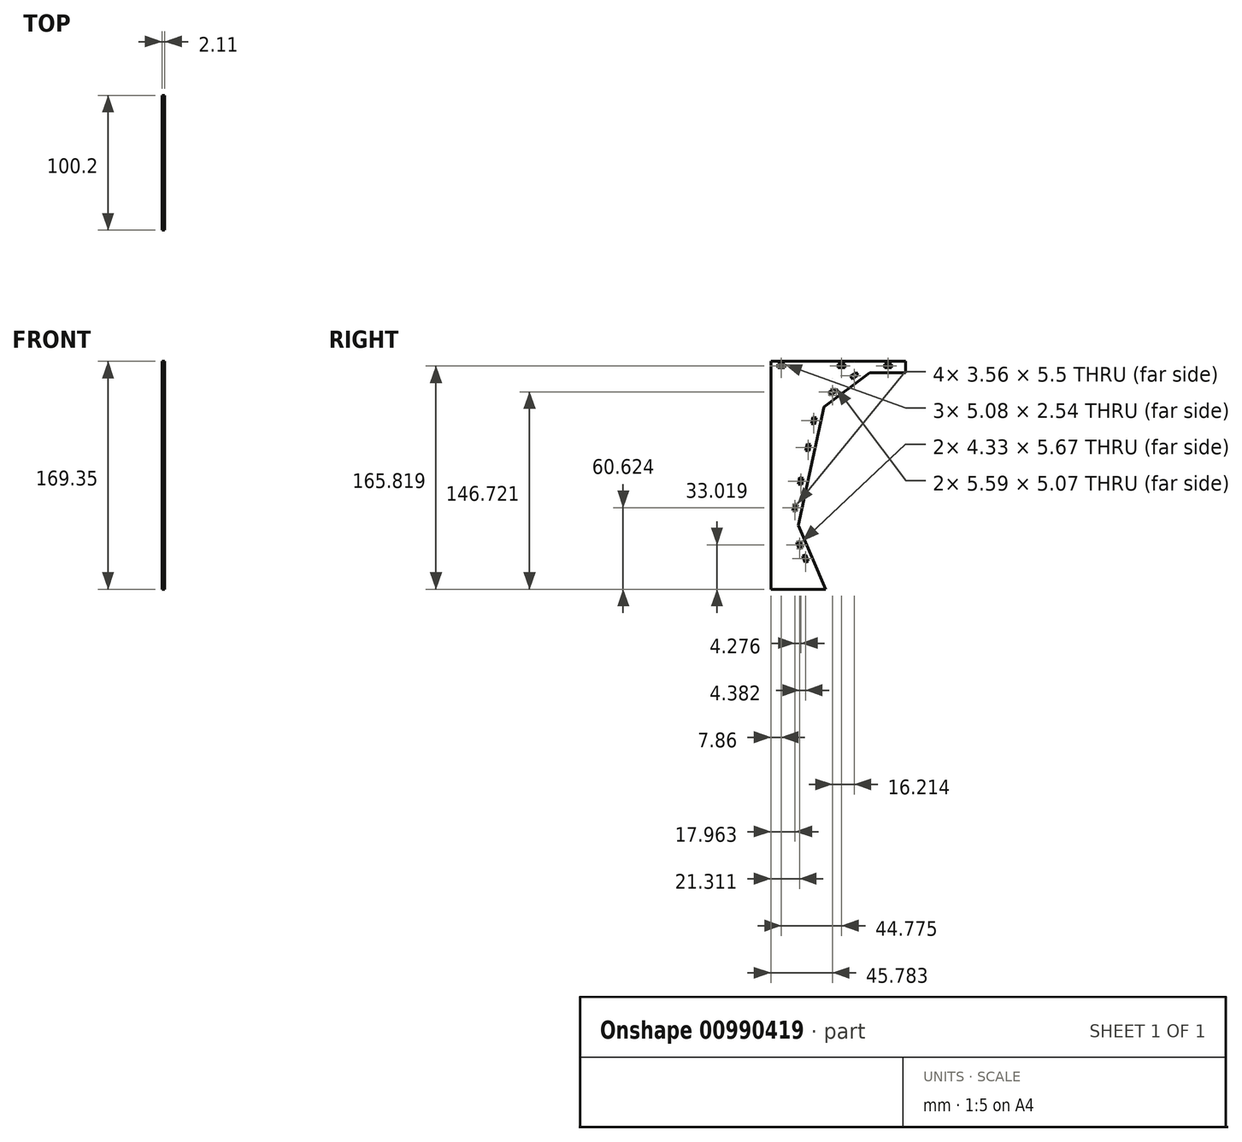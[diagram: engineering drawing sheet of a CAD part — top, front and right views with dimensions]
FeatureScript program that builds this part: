
annotation { "Feature Type Name" : "Feature", "Feature Type Description" : "" }
export const myFeature = defineFeature(function(context is Context, id is Id, definition is map)
    precondition{}
    {
        {
            var Q0;
            Q0=qCreatedBy(makeId("Right.planeOp"),FACE);
            var sketch = newSketch(context, id + "F0", { "sketchPlane" : qUnion([Q0])});
            skLineSegment(sketch, "E0", {"start": v(0, 0) * mm, "end": v(0, 169.34) * mm});
            skLineSegment(sketch, "E1", {"start": v(0, 169.34) * mm, "end": v(200.4, 169.34) * mm});
            skLineSegment(sketch, "E2", {"start": v(0, 0) * mm, "end": v(43.05, 0) * mm, "construction": true});
            skLineSegment(sketch, "E3", {"start": v(43.05, 0) * mm, "end": v(23.47, 45.96) * mm});
            skLineSegment(sketch, "E4", {"start": v(0, 47.82) * mm, "end": v(22.68, 47.82) * mm, "construction": true});
            skLineSegment(sketch, "E5", {"start": v(22.68, 47.82) * mm, "end": v(22.68, 0) * mm, "construction": true});
            skLineSegment(sketch, "E6", {"start": v(23.1, 49.8) * mm, "end": v(40.9, 132) * mm});
            skLineSegment(sketch, "E7", {"start": v(41.4, 134.33) * mm, "end": v(0, 134.33) * mm, "construction": true});
            skLineSegment(sketch, "E8", {"start": v(41.4, 134.33) * mm, "end": v(43.05, 0) * mm, "construction": true});
            skLineSegment(sketch, "E9", {"start": v(43.31, 135.75) * mm, "end": v(72.51, 157.5) * mm});
            skLineSegment(sketch, "E10", {"start": v(74.2, 158.76) * mm, "end": v(74.2, 169.34) * mm, "construction": true});
            skLineSegment(sketch, "E11", {"start": v(74.2, 158.76) * mm, "end": v(0, 158.76) * mm, "construction": true});
            skPoint(sketch, "E12", {"position": v(100.2, 169.34) * mm});
            skLineSegment(sketch, "E13", {"start": v(100.2, 169.34) * mm, "end": v(100.2, 154.3) * mm, "construction": true});
            skLineSegment(sketch, "E14", {"start": v(76.3, 158.76) * mm, "end": v(100.2, 158.76) * mm});
            skLineSegment(sketch, "E15.4", {"start": v(41.18, -0.8) * mm, "end": v(20.56, 47.62) * mm, "construction": true});
            skLineSegment(sketch, "E15.5", {"start": v(20.56, 47.62) * mm, "end": v(39.58, 135.5) * mm});
            skLineSegment(sketch, "E15.6", {"start": v(39.58, 135.5) * mm, "end": v(73.52, 160.79) * mm});
            skLineSegment(sketch, "E15.7", {"start": v(73.52, 160.79) * mm, "end": v(100.2, 160.79) * mm});
            skLineSegment(sketch, "E16.5", {"start": v(11.62, 46.77) * mm, "end": v(31.89, 140.45) * mm});
            skLineSegment(sketch, "E16.6", {"start": v(31.89, 140.45) * mm, "end": v(70.69, 169.35) * mm, "construction": true});
            skLineSegment(sketch, "E16.7", {"start": v(70.69, 169.35) * mm, "end": v(100.2, 169.35) * mm});
            skLineSegment(sketch, "E17", {"start": v(31.89, 140.45) * mm, "end": v(38.14, 169.34) * mm, "construction": true});
            skLineSegment(sketch, "E18", {"start": v(10.6, 158.76) * mm, "end": v(0, 158.76) * mm, "construction": true});
            skLineSegment(sketch, "E19", {"start": v(10.6, 158.76) * mm, "end": v(10.6, 46.77) * mm});
            skLineSegment(sketch, "E20", {"start": v(10.6, 46.77) * mm, "end": v(11.62, 46.77) * mm});
            skLineSegment(sketch, "E21", {"start": v(36.3, 160.79) * mm, "end": v(31.89, 140.45) * mm, "construction": true});
            skLineSegment(sketch, "E22", {"start": v(41.4, 134.33) * mm, "end": v(48.98, 169.34) * mm, "construction": true});
            skLineSegment(sketch, "E23", {"start": v(47.13, 160.79) * mm, "end": v(44.8, 150.07) * mm});
            skLineSegment(sketch, "E24", {"start": v(13.2, 0) * mm, "end": v(0, 0) * mm});
            skLineSegment(sketch, "E25", {"start": v(31.54, 0) * mm, "end": v(43.05, 0) * mm});
            skLineSegment(sketch, "E26", {"start": v(100.2, 158.76) * mm, "end": v(100.2, 169.35) * mm});
            skPoint(sketch, "E27", {"position": v(46.69, 158.76) * mm});
            skPoint(sketch, "E28", {"position": v(56.47, 158.76) * mm});
            skLineSegment(sketch, "E29", {"start": v(46.69, 158.76) * mm, "end": v(56.47, 158.76) * mm});
            skLineSegment(sketch, "E30", {"start": v(44.8, 150.07) * mm, "end": v(46.69, 158.76) * mm});
            skLineSegment(sketch, "E31", {"start": v(10.6, 158.76) * mm, "end": v(35.85, 158.76) * mm});
            skLineSegment(sketch, "E32", {"start": v(35.85, 158.76) * mm, "end": v(31.89, 140.45) * mm});
            skLineSegment(sketch, "E33", {"start": v(44.8, 150.07) * mm, "end": v(56.47, 158.76) * mm});
            skLineSegment(sketch, "E34", {"start": v(30.88, 85.7) * mm, "end": v(20.53, 87.94) * mm, "construction": true});
            skLineSegment(sketch, "E35.0", {"start": v(33.3, -4.15) * mm, "end": v(12.94, 43.67) * mm, "construction": true});
            skLineSegment(sketch, "E36", {"start": v(22.68, 47.82) * mm, "end": v(18.8, 29.9) * mm, "construction": true});
            skLineSegment(sketch, "E37", {"start": v(18.8, 29.9) * mm, "end": v(12.34, 0) * mm});
            skLineSegment(sketch, "E38", {"start": v(18.8, 29.9) * mm, "end": v(31.54, 0) * mm});
            skLineSegment(sketch, "E39", {"start": v(12.34, 0) * mm, "end": v(31.54, 0) * mm});
            skLineSegment(sketch, "E40", {"start": v(20.56, 47.62) * mm, "end": v(40.84, 0) * mm});
            skPoint(sketch, "E41.visualSharp", {"position": v(41.4, 134.33) * mm});
            skArc(sketch, "E41.filletArc", {"start": v(43.31, 135.75) * mm, "mid": v(41.77, 134.1) * mm, "end": v(40.9, 132) * mm});
            skPoint(sketch, "E42.visualSharp", {"position": v(22.68, 47.82) * mm});
            skArc(sketch, "E42.filletArc", {"start": v(23.1, 49.8) * mm, "mid": v(23, 47.85) * mm, "end": v(23.47, 45.96) * mm});
            skPoint(sketch, "E43.visualSharp", {"position": v(74.2, 158.76) * mm});
            skArc(sketch, "E43.filletArc", {"start": v(76.3, 158.76) * mm, "mid": v(74.3, 158.44) * mm, "end": v(72.51, 157.5) * mm});
            skPoint(sketch, "E44", {"position": v(21.75, 93.6) * mm});
            skLineSegment(sketch, "E45", {"start": v(21.75, 93.6) * mm, "end": v(22.1, 95.21) * mm});
            skLineSegment(sketch, "E46", {"start": v(22.1, 95.21) * mm, "end": v(26.54, 94.25) * mm});
            skLineSegment(sketch, "E47", {"start": v(29.56, 96.2) * mm, "end": v(37.5, 132.86) * mm});
            skLineSegment(sketch, "E48", {"start": v(35.55, 135.88) * mm, "end": v(31.1, 136.84) * mm});
            skPoint(sketch, "E49.visualSharp", {"position": v(38.03, 135.35) * mm});
            skArc(sketch, "E49.filletArc", {"start": v(37.5, 132.86) * mm, "mid": v(37.15, 134.78) * mm, "end": v(35.55, 135.88) * mm});
            skPoint(sketch, "E50.visualSharp", {"position": v(29.02, 93.72) * mm});
            skArc(sketch, "E50.filletArc", {"start": v(26.54, 94.25) * mm, "mid": v(28.45, 94.6) * mm, "end": v(29.56, 96.2) * mm});
            skLineSegment(sketch, "E51", {"start": v(21.75, 93.6) * mm, "end": v(32.1, 91.37) * mm, "construction": true});
            skLineSegment(sketch, "E52.0", {"start": v(35.01, 133.4) * mm, "end": v(30.57, 134.36) * mm});
            skLineSegment(sketch, "E52.1", {"start": v(22.64, 97.7) * mm, "end": v(27.08, 96.74) * mm});
            skLineSegment(sketch, "E52.2", {"start": v(27.08, 96.74) * mm, "end": v(27.08, 96.74) * mm});
            skLineSegment(sketch, "E52.3", {"start": v(27.08, 96.74) * mm, "end": v(35.01, 133.4) * mm});
            skLineSegment(sketch, "E52.4", {"start": v(35.01, 133.4) * mm, "end": v(35.01, 133.4) * mm});
            skLineSegment(sketch, "E53.MirrorCS", {"start": v(21.4, 92) * mm, "end": v(25.85, 91.04) * mm});
            skArc(sketch, "E54.MirrorCS", {"start": v(25.85, 91.04) * mm, "mid": v(27.44, 89.94) * mm, "end": v(27.8, 88.02) * mm});
            skLineSegment(sketch, "E55.MirrorCS", {"start": v(27.8, 88.02) * mm, "end": v(19.86, 51.36) * mm});
            skArc(sketch, "E56.MirrorCS", {"start": v(19.86, 51.36) * mm, "mid": v(18.75, 49.76) * mm, "end": v(16.84, 49.41) * mm});
            skLineSegment(sketch, "E57.MirrorCS", {"start": v(16.84, 49.41) * mm, "end": v(12.4, 50.38) * mm});
            skLineSegment(sketch, "E58.MirrorCS", {"start": v(17.37, 51.9) * mm, "end": v(12.94, 52.86) * mm});
            skLineSegment(sketch, "E59.MirrorCS", {"start": v(25.3, 88.56) * mm, "end": v(17.37, 51.9) * mm});
            skLineSegment(sketch, "E60.MirrorCS", {"start": v(20.87, 89.52) * mm, "end": v(25.3, 88.56) * mm});
            skLineSegment(sketch, "E61", {"start": v(33.72, 127.42) * mm, "end": v(31.23, 127.96) * mm});
            skLineSegment(sketch, "E62", {"start": v(31.23, 127.96) * mm, "end": v(30.16, 123) * mm});
            skLineSegment(sketch, "E63", {"start": v(30.16, 123) * mm, "end": v(32.64, 122.46) * mm});
            skLineSegment(sketch, "E64", {"start": v(28.37, 102.7) * mm, "end": v(25.88, 103.24) * mm});
            skLineSegment(sketch, "E65", {"start": v(25.88, 103.24) * mm, "end": v(26.96, 108.2) * mm});
            skLineSegment(sketch, "E66", {"start": v(26.96, 108.2) * mm, "end": v(29.44, 107.66) * mm});
            skLineSegment(sketch, "E67.MirrorCS", {"start": v(24.02, 82.6) * mm, "end": v(21.54, 83.13) * mm});
            skLineSegment(sketch, "E68.MirrorCS", {"start": v(21.54, 83.13) * mm, "end": v(20.46, 78.17) * mm});
            skLineSegment(sketch, "E69.MirrorCS", {"start": v(20.46, 78.17) * mm, "end": v(22.94, 77.63) * mm});
            skLineSegment(sketch, "E70.MirrorCS", {"start": v(17.26, 63.37) * mm, "end": v(19.74, 62.84) * mm});
            skLineSegment(sketch, "E71.MirrorCS", {"start": v(16.19, 58.4) * mm, "end": v(17.26, 63.37) * mm});
            skLineSegment(sketch, "E72.MirrorCS", {"start": v(18.67, 57.87) * mm, "end": v(16.19, 58.4) * mm});
            skLineSegment(sketch, "E73", {"start": v(31.89, 140.45) * mm, "end": v(41.4, 134.33) * mm, "construction": true});
            skLineSegment(sketch, "E74.MirrorCS", {"start": v(37.56, 139.02) * mm, "end": v(34.85, 142.66) * mm});
            skArc(sketch, "E75.MirrorCS", {"start": v(41.12, 138.5) * mm, "mid": v(39.23, 138.02) * mm, "end": v(37.56, 139.02) * mm});
            skLineSegment(sketch, "E76.MirrorCS", {"start": v(71.2, 160.9) * mm, "end": v(41.12, 138.5) * mm});
            skArc(sketch, "E77.MirrorCS", {"start": v(71.72, 164.46) * mm, "mid": v(72.2, 162.57) * mm, "end": v(71.2, 160.9) * mm});
            skLineSegment(sketch, "E78.MirrorCS", {"start": v(69, 168.1) * mm, "end": v(71.72, 164.46) * mm});
            skLineSegment(sketch, "E79.MirrorCS", {"start": v(66.97, 166.58) * mm, "end": v(69.69, 162.94) * mm});
            skLineSegment(sketch, "E80.MirrorCS", {"start": v(69.69, 162.94) * mm, "end": v(39.6, 140.53) * mm});
            skLineSegment(sketch, "E81.MirrorCS", {"start": v(64.8, 159.3) * mm, "end": v(63.28, 161.33) * mm});
            skLineSegment(sketch, "E82.MirrorCS", {"start": v(63.28, 161.33) * mm, "end": v(59.2, 158.3) * mm});
            skLineSegment(sketch, "E83.MirrorCS", {"start": v(59.2, 158.3) * mm, "end": v(60.72, 156.26) * mm});
            skLineSegment(sketch, "E84.MirrorCS", {"start": v(47.06, 149.26) * mm, "end": v(48.58, 147.22) * mm});
            skLineSegment(sketch, "E85.MirrorCS", {"start": v(42.99, 146.22) * mm, "end": v(47.06, 149.26) * mm});
            skLineSegment(sketch, "E86.MirrorCS", {"start": v(44.5, 144.19) * mm, "end": v(42.99, 146.22) * mm});
            skLineSegment(sketch, "E87.MirrorCS", {"start": v(39.6, 140.53) * mm, "end": v(36.89, 144.18) * mm});
            skLineSegment(sketch, "E88", {"start": v(70.69, 169.35) * mm, "end": v(70.69, 164.55) * mm});
            skLineSegment(sketch, "E89", {"start": v(68.15, 162) * mm, "end": v(0, 162) * mm});
            skPoint(sketch, "E90.visualSharp", {"position": v(70.69, 162) * mm});
            skArc(sketch, "E90.filletArc", {"start": v(68.15, 162) * mm, "mid": v(69.94, 162.75) * mm, "end": v(70.69, 164.55) * mm});
            skLineSegment(sketch, "E91.0", {"start": v(68.15, 164.55) * mm, "end": v(0, 164.55) * mm});
            skLineSegment(sketch, "E91.1", {"start": v(68.15, 169.63) * mm, "end": v(68.15, 164.55) * mm});
            skLineSegment(sketch, "E92", {"start": v(55.17, 164.55) * mm, "end": v(55.17, 167.09) * mm});
            skLineSegment(sketch, "E93", {"start": v(55.17, 167.09) * mm, "end": v(50.1, 167.09) * mm});
            skLineSegment(sketch, "E94", {"start": v(50.1, 167.09) * mm, "end": v(50.1, 164.55) * mm});
            skLineSegment(sketch, "E95", {"start": v(10.4, 164.55) * mm, "end": v(10.4, 167.09) * mm});
            skLineSegment(sketch, "E96", {"start": v(10.4, 167.09) * mm, "end": v(5.32, 167.09) * mm});
            skLineSegment(sketch, "E97", {"start": v(5.32, 167.09) * mm, "end": v(5.32, 164.55) * mm});
            skLineSegment(sketch, "E98", {"start": v(22.68, 47.82) * mm, "end": v(11.62, 46.77) * mm, "construction": true});
            skLineSegment(sketch, "E99", {"start": v(15.36, 37.97) * mm, "end": v(19.78, 39.85) * mm});
            skLineSegment(sketch, "E100", {"start": v(23.11, 38.51) * mm, "end": v(37.3, 5.2) * mm});
            skLineSegment(sketch, "E101", {"start": v(35.96, 1.87) * mm, "end": v(31.54, -0.01) * mm});
            skPoint(sketch, "E102.visualSharp", {"position": v(38.3, 2.87) * mm});
            skArc(sketch, "E102.filletArc", {"start": v(35.96, 1.87) * mm, "mid": v(37.32, 3.26) * mm, "end": v(37.3, 5.2) * mm});
            skPoint(sketch, "E103.visualSharp", {"position": v(22.12, 40.85) * mm});
            skArc(sketch, "E103.filletArc", {"start": v(23.11, 38.51) * mm, "mid": v(21.72, 39.87) * mm, "end": v(19.78, 39.85) * mm});
            skLineSegment(sketch, "E104.0", {"start": v(34.97, 4.2) * mm, "end": v(25.52, 0.18) * mm});
            skLineSegment(sketch, "E104.1", {"start": v(20.78, 37.52) * mm, "end": v(34.97, 4.2) * mm});
            skLineSegment(sketch, "E104.2", {"start": v(16.36, 35.63) * mm, "end": v(20.78, 37.52) * mm});
            skLineSegment(sketch, "E105", {"start": v(27.86, 20.9) * mm, "end": v(25.52, 19.9) * mm});
            skLineSegment(sketch, "E106", {"start": v(25.52, 19.9) * mm, "end": v(23.53, 24.57) * mm});
            skLineSegment(sketch, "E107", {"start": v(23.53, 24.57) * mm, "end": v(25.87, 25.57) * mm});
            skLineSegment(sketch, "E108", {"start": v(21.48, 35.85) * mm, "end": v(19.15, 34.86) * mm});
            skLineSegment(sketch, "E109", {"start": v(19.15, 34.86) * mm, "end": v(21.14, 30.18) * mm});
            skLineSegment(sketch, "E110", {"start": v(21.14, 30.18) * mm, "end": v(23.48, 31.18) * mm});
            skLineSegment(sketch, "E111", {"start": v(79.6, 169.35) * mm, "end": v(79.6, 164.55) * mm});
            skLineSegment(sketch, "E112", {"start": v(82.14, 162) * mm, "end": v(100.2, 162) * mm});
            skPoint(sketch, "E113.visualSharp", {"position": v(79.6, 162) * mm});
            skArc(sketch, "E113.filletArc", {"start": v(79.6, 164.55) * mm, "mid": v(80.34, 162.75) * mm, "end": v(82.14, 162) * mm});
            skLineSegment(sketch, "E114.0", {"start": v(82.14, 164.55) * mm, "end": v(100.2, 164.55) * mm});
            skLineSegment(sketch, "E114.1", {"start": v(82.14, 169.35) * mm, "end": v(82.14, 164.55) * mm});
            skLineSegment(sketch, "E115", {"start": v(84.57, 164.55) * mm, "end": v(84.57, 167.09) * mm});
            skPoint(sketch, "E115.endSnap0", {"position": v(68.15, 167.09) * mm});
            skLineSegment(sketch, "E116", {"start": v(84.57, 167.09) * mm, "end": v(89.65, 167.09) * mm});
            skLineSegment(sketch, "E117", {"start": v(89.65, 167.09) * mm, "end": v(89.65, 164.55) * mm});
            skSolve(sketch);
        }
        {
            var Q0;
            Q0=makeQuery(id+"F0.imprint","IMPRINT",FACE,{"disambiguationData":[TD([[makeQuery(id+"F0.imprint","IMPRINT",EDGE,{"derivedFrom":sQuery(id+"F0.wireOp",EDGE,"E19")}),1.0]])]});
            var Q1;
            {var subQ3=sQuery(id+"F0.wireOp",EDGE,"E52.0");Q1=makeQuery(id+"F0.imprint","IMPRINT",FACE,{"disambiguationData":[TD([[makeQuery(id+"F0.imprint","IMPRINT",EDGE,{"derivedFrom":subQ3}),1.0]])]});}
            var Q2;
            {var subQ5=sQuery(id+"F0.wireOp",EDGE,"E46");Q2=makeQuery(id+"F0.imprint","IMPRINT",FACE,{"disambiguationData":[TD([[makeQuery(id+"F0.imprint","IMPRINT",EDGE,{"derivedFrom":subQ5}),1.0]])]});}
            var Q3;
            {var subQ4=sQuery(id+"F0.wireOp",EDGE,"E58.MirrorCS");Q3=makeQuery(id+"F0.imprint","IMPRINT",FACE,{"disambiguationData":[TD([[makeQuery(id+"F0.imprint","IMPRINT",EDGE,{"derivedFrom":subQ4}),-1.0]])]});}
            var Q4;
            {var subQ7=sQuery(id+"F0.wireOp",EDGE,"E53.MirrorCS");Q4=makeQuery(id+"F0.imprint","IMPRINT",FACE,{"disambiguationData":[TD([[makeQuery(id+"F0.imprint","IMPRINT",EDGE,{"derivedFrom":subQ7}),-1.0]])]});}
            var Q5;
            {var subQ0=sQuery(id+"F0.wireOp",EDGE,"E37");Q5=makeQuery(id+"F0.imprint","IMPRINT",FACE,{"disambiguationData":[TD([[makeQuery(id+"F0.imprint","IMPRINT",EDGE,{"derivedFrom":subQ0}),1.0]])]});}
            var Q6;
            {var subQ0=sQuery(id+"F0.wireOp",EDGE,"E88");var subQ1=sQuery(id+"F0.wireOp",EDGE,"E1");var subQ2=makeQuery(id+"F0.imprint","INTERSECT",VERTEX,{"derivedFrom":[subQ1,subQ0]});Q6=makeQuery(id+"F0.imprint","IMPRINT",FACE,{"disambiguationData":[TD([[makeQuery(id+"F0.imprint","IMPRINT",EDGE,{"disambiguationData":[TD([[subQ2,-1.0]])],"derivedFrom":subQ1}),1.0]])]});}
            var Q7;
            {var subQ0=sQuery(id+"F0.wireOp",EDGE,"E26");var subQ1=sQuery(id+"F0.wireOp",EDGE,"E1");var subQ2=makeQuery(id+"F0.imprint","INTERSECT",VERTEX,{"derivedFrom":[subQ1,subQ0]});Q7=makeQuery(id+"F0.imprint","IMPRINT",FACE,{"disambiguationData":[TD([[makeQuery(id+"F0.imprint","IMPRINT",EDGE,{"disambiguationData":[TD([[subQ2,1.0]])],"derivedFrom":subQ1}),1.0]])]});}
            var Q8;
            {var subQ0=sQuery(id+"F0.wireOp",EDGE,"E88");var subQ1=makeQuery(id+"F0.imprint","IMPRINT",VERTEX,{"derivedFrom":subQ0});Q8=makeQuery(id+"F0.imprint","IMPRINT",FACE,{"disambiguationData":[TD([[makeQuery(id+"F0.imprint","IMPRINT",EDGE,{"disambiguationData":[TD([[subQ1,1.0]])],"derivedFrom":subQ0}),-1.0]])]});}
            var Q9;
            {var subQ0=sQuery(id+"F0.wireOp",EDGE,"E111");var subQ1=sQuery(id+"F0.wireOp",EDGE,"E1");var subQ2=makeQuery(id+"F0.imprint","INTERSECT",VERTEX,{"derivedFrom":[subQ1,subQ0]});Q9=makeQuery(id+"F0.imprint","IMPRINT",FACE,{"disambiguationData":[TD([[makeQuery(id+"F0.imprint","IMPRINT",EDGE,{"disambiguationData":[TD([[subQ2,-1.0]])],"derivedFrom":subQ1}),1.0]])]});}
            var Q10;
            {var subQ3=sQuery(id+"F0.wireOp",EDGE,"E115");Q10=makeQuery(id+"F0.imprint","IMPRINT",FACE,{"disambiguationData":[TD([[makeQuery(id+"F0.imprint","IMPRINT",EDGE,{"derivedFrom":subQ3}),1.0]])]});}
            var Q11;
            {var subQ0=sQuery(id+"F0.wireOp",EDGE,"E92");Q11=makeQuery(id+"F0.imprint","IMPRINT",FACE,{"disambiguationData":[TD([[makeQuery(id+"F0.imprint","IMPRINT",EDGE,{"derivedFrom":subQ0}),-1.0]])]});}
            var Q12;
            {var subQ4=sQuery(id+"F0.wireOp",EDGE,"E112");Q12=makeQuery(id+"F0.imprint","IMPRINT",FACE,{"disambiguationData":[TD([[makeQuery(id+"F0.imprint","IMPRINT",EDGE,{"derivedFrom":subQ4}),1.0]])]});}
            var Q13;
            {var subQ10=sQuery(id+"F0.wireOp",EDGE,"E89");Q13=makeQuery(id+"F0.imprint","IMPRINT",FACE,{"disambiguationData":[TD([[makeQuery(id+"F0.imprint","IMPRINT",EDGE,{"derivedFrom":subQ10}),-1.0]])]});}
            var Q14;
            Q14=makeQuery(id+"F0.imprint","IMPRINT",FACE,{"disambiguationData":[TD([[makeQuery(id+"F0.imprint","IMPRINT",EDGE,{"derivedFrom":sQuery(id+"F0.wireOp",EDGE,"E15.5")}),1.0]])]});
            var Q15;
            Q15=makeQuery(id+"F0.imprint","IMPRINT",FACE,{"disambiguationData":[TD([[makeQuery(id+"F0.imprint","IMPRINT",EDGE,{"derivedFrom":sQuery(id+"F0.wireOp",EDGE,"E29")}),-1.0]])]});
            extrude(context, id + "F1", {"entities" : qUnion([Q0, Q1, Q2, Q3, Q4, Q5, Q6, Q7, Q8, Q9, Q10, Q11, Q12, Q13, Q14, Q15]), "depth" : 2.1 * mm, "offsetDistance" : 25.4 * mm});
        }
    });
